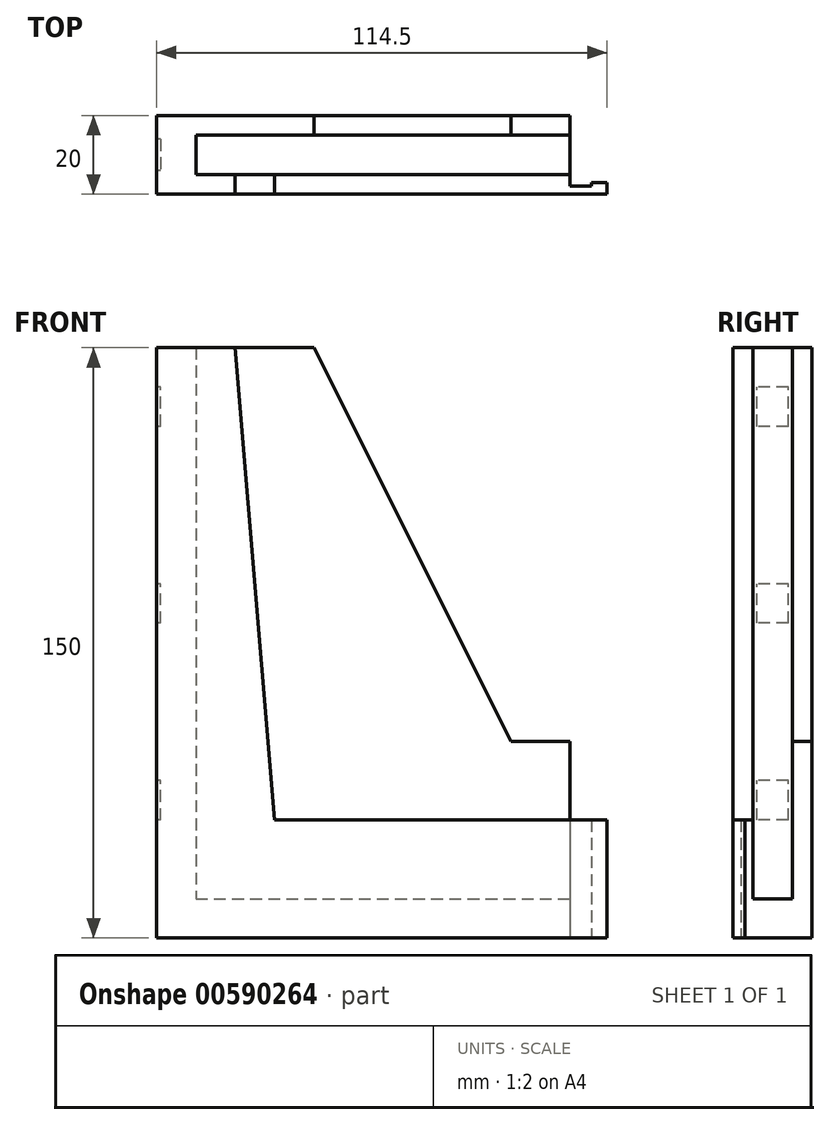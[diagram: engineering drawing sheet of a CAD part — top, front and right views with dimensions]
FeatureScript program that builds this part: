
annotation { "Feature Type Name" : "Feature", "Feature Type Description" : "" }
export const myFeature = defineFeature(function(context is Context, id is Id, definition is map)
    precondition{}
    {
        {
            var Q0;
            Q0=qCreatedBy(makeId("Top.planeOp"),FACE);
            var sketch = newSketch(context, id + "F0", { "sketchPlane" : qUnion([Q0])});
            skLineSegment(sketch, "E0.bottom", {"start": v(0, 0) * mm, "end": v(10, 0) * mm});
            skLineSegment(sketch, "E0.top", {"start": v(0, 20) * mm, "end": v(10, 20) * mm});
            skLineSegment(sketch, "E0.left", {"start": v(0, 0) * mm, "end": v(0, 20) * mm});
            skLineSegment(sketch, "E0.right", {"start": v(10, 0) * mm, "end": v(10, 20) * mm});
            skLineSegment(sketch, "E1.bottom", {"start": v(10, 20) * mm, "end": v(40, 20) * mm});
            skLineSegment(sketch, "E1.top", {"start": v(10, 15) * mm, "end": v(40, 15) * mm});
            skLineSegment(sketch, "E1.left", {"start": v(10, 20) * mm, "end": v(10, 15) * mm});
            skLineSegment(sketch, "E1.right", {"start": v(40, 20) * mm, "end": v(40, 15) * mm});
            skSolve(sketch);
        }
        {
            var Q0;
            Q0 = qSketchRegion(id + "F0", true);
            extrude(context, id + "F1", {"entities" : qUnion([Q0]), "depth" : 150 * mm, "offsetDistance" : 25 * mm});
        }
        {
            var Q0;
            Q0=qCreatedBy(makeId("Top.planeOp"),FACE);
            var sketch = newSketch(context, id + "F2", { "sketchPlane" : qUnion([Q0])});
            skLineSegment(sketch, "E2.bottom", {"start": v(10, 0) * mm, "end": v(105, 0) * mm});
            skLineSegment(sketch, "E2.top", {"start": v(10, 5) * mm, "end": v(105, 5) * mm});
            skLineSegment(sketch, "E2.left", {"start": v(10, 0) * mm, "end": v(10, 5) * mm});
            skLineSegment(sketch, "E2.right", {"start": v(105, 0) * mm, "end": v(105, 5) * mm});
            skSolve(sketch);
        }
        {
            var Q0;
            Q0 = qSketchRegion(id + "F2", true);
            extrude(context, id + "F3", {"entities" : qUnion([Q0]), "operationType" : NewBodyOperationType.ADD, "depth" : 30 * mm, "offsetDistance" : 25 * mm});
        }
        {
            var Q0;
            Q0=makeQuery(id+"F3.opExtrude","CAP_FACE",FACE,{"disambiguationData":[OSD([sQuery(id+"F2.wireOp",EDGE,"E2.bottom"),sQuery(id+"F2.wireOp",EDGE,"E2.top"),sQuery(id+"F2.wireOp",EDGE,"E2.left"),sQuery(id+"F2.wireOp",EDGE,"E2.right")])],"isStart":false});
            var sketch = newSketch(context, id + "F4", { "sketchPlane" : qUnion([Q0])});
            skLineSegment(sketch, "E3.bottom", {"start": v(10, 5) * mm, "end": v(20, 5) * mm});
            skLineSegment(sketch, "E3.top", {"start": v(10, 0) * mm, "end": v(20, 0) * mm});
            skLineSegment(sketch, "E3.left", {"start": v(10, 5) * mm, "end": v(10, 0) * mm});
            skLineSegment(sketch, "E3.right", {"start": v(20, 5) * mm, "end": v(20, 0) * mm});
            skSolve(sketch);
        }
        {
            var Q0;
            Q0 = qSketchRegion(id + "F4", true);
            extrude(context, id + "F5", {"entities" : qUnion([Q0]), "operationType" : NewBodyOperationType.ADD, "depth" : 120 * mm, "offsetDistance" : 25 * mm});
        }
        {
            var Q0;
            Q0=makeQuery(id+"F5.boolean.opBoolean","MERGE",FACE,{"derivedFrom":[makeQuery(id+"F3.boolean.opBoolean","MERGE",FACE,{"derivedFrom":[makeQuery(id+"F1.opExtrude","SWEPT_FACE",FACE,{"disambiguationData":[OSD([sQuery(id+"F0.wireOp",EDGE,"E0.bottom")])]}),makeQuery(id+"F3.opExtrude","SWEPT_FACE",FACE,{"disambiguationData":[OSD([sQuery(id+"F2.wireOp",EDGE,"E2.bottom")])]})]}),makeQuery(id+"F5.opExtrude","SWEPT_FACE",FACE,{"disambiguationData":[OSD([sQuery(id+"F4.wireOp",EDGE,"E3.top")])]})]});
            var sketch = newSketch(context, id + "F6", { "sketchPlane" : qUnion([Q0])});
            skLineSegment(sketch, "E4", {"start": v(20, 150) * mm, "end": v(20, 30) * mm});
            skLineSegment(sketch, "E5", {"start": v(20, 30) * mm, "end": v(30, 30) * mm});
            skLineSegment(sketch, "E6", {"start": v(30, 30) * mm, "end": v(20, 150) * mm});
            skSolve(sketch);
        }
        {
            var Q0;
            Q0 = qSketchRegion(id + "F6", true);
            extrude(context, id + "F7", {"entities" : qUnion([Q0]), "operationType" : NewBodyOperationType.ADD, "oppositeDirection" : true, "depth" : 5 * mm, "offsetDistance" : 25 * mm});
        }
        {
            var Q0;
            Q0=qCreatedBy(makeId("Top.planeOp"),FACE);
            var sketch = newSketch(context, id + "F8", { "sketchPlane" : qUnion([Q0])});
            skLineSegment(sketch, "E7.bottom", {"start": v(40, 20) * mm, "end": v(105, 20) * mm});
            skLineSegment(sketch, "E7.top", {"start": v(40, 15) * mm, "end": v(105, 15) * mm});
            skLineSegment(sketch, "E7.left", {"start": v(40, 20) * mm, "end": v(40, 15) * mm});
            skLineSegment(sketch, "E7.right", {"start": v(105, 20) * mm, "end": v(105, 15) * mm});
            skSolve(sketch);
        }
        {
            var Q0;
            Q0 = qSketchRegion(id + "F8", true);
            extrude(context, id + "F9", {"entities" : qUnion([Q0]), "operationType" : NewBodyOperationType.ADD, "depth" : 50 * mm, "offsetDistance" : 25 * mm});
        }
        {
            var Q0;
            Q0=makeQuery(id+"F9.boolean.opBoolean","MERGE",FACE,{"derivedFrom":[makeQuery(id+"F1.opExtrude","SWEPT_FACE",FACE,{"disambiguationData":[OSD([sQuery(id+"F0.wireOp",EDGE,"E0.top"),sQuery(id+"F0.wireOp",EDGE,"E1.bottom")])]}),makeQuery(id+"F9.opExtrude","SWEPT_FACE",FACE,{"disambiguationData":[OSD([sQuery(id+"F8.wireOp",EDGE,"E7.bottom")])]})]});
            var sketch = newSketch(context, id + "F10", { "sketchPlane" : qUnion([Q0])});
            skLineSegment(sketch, "E8", {"start": v(-40, 50) * mm, "end": v(-40, 150) * mm});
            skLineSegment(sketch, "E9", {"start": v(-40, 150) * mm, "end": v(-90, 50) * mm});
            skLineSegment(sketch, "E10", {"start": v(-90, 50) * mm, "end": v(-40, 50) * mm});
            skSolve(sketch);
        }
        {
            var Q0;
            Q0 = qSketchRegion(id + "F10", true);
            extrude(context, id + "F11", {"entities" : qUnion([Q0]), "operationType" : NewBodyOperationType.ADD, "oppositeDirection" : true, "depth" : 5 * mm, "offsetDistance" : 25 * mm});
        }
        {
            var Q0;
            Q0=qCreatedBy(makeId("Top.planeOp"),FACE);
            var sketch = newSketch(context, id + "F12", { "sketchPlane" : qUnion([Q0])});
            skLineSegment(sketch, "E11.bottom", {"start": v(10, 5) * mm, "end": v(105, 5) * mm});
            skLineSegment(sketch, "E11.top", {"start": v(10, 15) * mm, "end": v(105, 15) * mm});
            skLineSegment(sketch, "E11.left", {"start": v(10, 5) * mm, "end": v(10, 15) * mm});
            skLineSegment(sketch, "E11.right", {"start": v(105, 5) * mm, "end": v(105, 15) * mm});
            skSolve(sketch);
        }
        {
            var Q0;
            Q0 = qSketchRegion(id + "F12", true);
            extrude(context, id + "F13", {"entities" : qUnion([Q0]), "operationType" : NewBodyOperationType.ADD, "depth" : 10 * mm, "offsetDistance" : 25 * mm});
        }
        {
            var Q0;
            Q0=makeQuery(id+"F7.boolean.opBoolean","MERGE",FACE,{"derivedFrom":[makeQuery(id+"F5.boolean.opBoolean","MERGE",FACE,{"derivedFrom":[makeQuery(id+"F3.boolean.opBoolean","MERGE",FACE,{"derivedFrom":[makeQuery(id+"F1.opExtrude","SWEPT_FACE",FACE,{"disambiguationData":[OSD([sQuery(id+"F0.wireOp",EDGE,"E0.bottom")])]}),makeQuery(id+"F3.opExtrude","SWEPT_FACE",FACE,{"disambiguationData":[OSD([sQuery(id+"F2.wireOp",EDGE,"E2.bottom")])]})]}),makeQuery(id+"F5.opExtrude","SWEPT_FACE",FACE,{"disambiguationData":[OSD([sQuery(id+"F4.wireOp",EDGE,"E3.top")])]})]}),makeQuery(id+"F7.opExtrude","CAP_FACE",FACE,{"disambiguationData":[OSD([sQuery(id+"F6.wireOp",EDGE,"E4"),sQuery(id+"F6.wireOp",EDGE,"E5"),sQuery(id+"F6.wireOp",EDGE,"E6")])],"isStart":true})]});
            var sketch = newSketch(context, id + "F14", { "sketchPlane" : qUnion([Q0])});
            skLineSegment(sketch, "E12.bottom", {"start": v(105, 30) * mm, "end": v(110.5, 30) * mm});
            skLineSegment(sketch, "E12.top", {"start": v(105, 0) * mm, "end": v(110.5, 0) * mm});
            skLineSegment(sketch, "E12.left", {"start": v(105, 30) * mm, "end": v(105, 0) * mm});
            skLineSegment(sketch, "E12.right", {"start": v(110.5, 30) * mm, "end": v(110.5, 0) * mm});
            skSolve(sketch);
        }
        {
            var Q0;
            Q0 = qSketchRegion(id + "F14", true);
            extrude(context, id + "F15", {"entities" : qUnion([Q0]), "operationType" : NewBodyOperationType.ADD, "oppositeDirection" : true, "depth" : 2 * mm, "offsetDistance" : 25 * mm});
        }
        {
            var Q0;
            Q0=makeQuery(id+"F15.boolean.opBoolean","MERGE",FACE,{"derivedFrom":[makeQuery(id+"F7.boolean.opBoolean","MERGE",FACE,{"derivedFrom":[makeQuery(id+"F5.boolean.opBoolean","MERGE",FACE,{"derivedFrom":[makeQuery(id+"F3.boolean.opBoolean","MERGE",FACE,{"derivedFrom":[makeQuery(id+"F1.opExtrude","SWEPT_FACE",FACE,{"disambiguationData":[OSD([sQuery(id+"F0.wireOp",EDGE,"E0.bottom")])]}),makeQuery(id+"F3.opExtrude","SWEPT_FACE",FACE,{"disambiguationData":[OSD([sQuery(id+"F2.wireOp",EDGE,"E2.bottom")])]})]}),makeQuery(id+"F5.opExtrude","SWEPT_FACE",FACE,{"disambiguationData":[OSD([sQuery(id+"F4.wireOp",EDGE,"E3.top")])]})]}),makeQuery(id+"F7.opExtrude","CAP_FACE",FACE,{"disambiguationData":[OSD([sQuery(id+"F6.wireOp",EDGE,"E4"),sQuery(id+"F6.wireOp",EDGE,"E5"),sQuery(id+"F6.wireOp",EDGE,"E6")])],"isStart":true})]}),makeQuery(id+"F15.opExtrude","CAP_FACE",FACE,{"disambiguationData":[OSD([sQuery(id+"F14.wireOp",EDGE,"E12.bottom"),sQuery(id+"F14.wireOp",EDGE,"E12.top"),sQuery(id+"F14.wireOp",EDGE,"E12.left"),sQuery(id+"F14.wireOp",EDGE,"E12.right")])],"isStart":true})]});
            var sketch = newSketch(context, id + "F16", { "sketchPlane" : qUnion([Q0])});
            skLineSegment(sketch, "E13.bottom", {"start": v(110.5, 30) * mm, "end": v(114.5, 30) * mm});
            skLineSegment(sketch, "E13.top", {"start": v(110.5, 0) * mm, "end": v(114.5, 0) * mm});
            skLineSegment(sketch, "E13.left", {"start": v(110.5, 30) * mm, "end": v(110.5, 0) * mm});
            skLineSegment(sketch, "E13.right", {"start": v(114.5, 30) * mm, "end": v(114.5, 0) * mm});
            skSolve(sketch);
        }
        {
            var Q0;
            Q0 = qSketchRegion(id + "F16", true);
            extrude(context, id + "F17", {"entities" : qUnion([Q0]), "operationType" : NewBodyOperationType.ADD, "oppositeDirection" : true, "depth" : 3 * mm, "offsetDistance" : 25 * mm});
        }
        {
            var Q0;
            Q0=makeQuery(id+"F1.opExtrude","SWEPT_FACE",FACE,{"disambiguationData":[OSD([sQuery(id+"F0.wireOp",EDGE,"E0.left")])]});
            var sketch = newSketch(context, id + "F18", { "sketchPlane" : qUnion([Q0])});
            skLineSegment(sketch, "E14.bottom", {"start": v(-14, 30) * mm, "end": v(-6, 30) * mm});
            skLineSegment(sketch, "E14.top", {"start": v(-14, 40) * mm, "end": v(-6, 40) * mm});
            skLineSegment(sketch, "E14.left", {"start": v(-14, 30) * mm, "end": v(-14, 40) * mm});
            skLineSegment(sketch, "E14.right", {"start": v(-6, 30) * mm, "end": v(-6, 40) * mm});
            skLineSegment(sketch, "E15.bottom", {"start": v(-14, 80) * mm, "end": v(-6, 80) * mm});
            skLineSegment(sketch, "E15.top", {"start": v(-14, 90) * mm, "end": v(-6, 90) * mm});
            skLineSegment(sketch, "E15.left", {"start": v(-14, 80) * mm, "end": v(-14, 90) * mm});
            skLineSegment(sketch, "E15.right", {"start": v(-6, 80) * mm, "end": v(-6, 90) * mm});
            skLineSegment(sketch, "E16.bottom", {"start": v(-14, 130) * mm, "end": v(-6, 130) * mm});
            skLineSegment(sketch, "E16.top", {"start": v(-14, 140) * mm, "end": v(-6, 140) * mm});
            skLineSegment(sketch, "E16.left", {"start": v(-14, 130) * mm, "end": v(-14, 140) * mm});
            skLineSegment(sketch, "E16.right", {"start": v(-6, 130) * mm, "end": v(-6, 140) * mm});
            skSolve(sketch);
        }
        {
            var Q0;
            Q0 = qSketchRegion(id + "F18", true);
            extrude(context, id + "F19", {"entities" : qUnion([Q0]), "operationType" : NewBodyOperationType.REMOVE, "oppositeDirection" : true, "depth" : 1 * mm, "offsetDistance" : 25 * mm});
        }
    });
